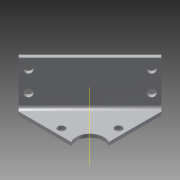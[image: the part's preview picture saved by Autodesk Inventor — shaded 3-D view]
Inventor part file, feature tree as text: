
AUTODESK INVENTOR PART (.ipt)
format: ipt  version: 2013 (Build 170138000, 138)  size: 141,824 bytes
history: native  units: in
note: dims shown in document units (in); Inventor stores cm internally (conversion verified against a paired STEP export)
features: sheet_metal_op x4, other x4, sketch x3
ambient origin geometry x8: Origin, YZ Plane, XZ Plane, XY Plane, X Axis, Y Axis, Z Axis, Center Point
bodies: Solid1 (feature_tree)
feature tree (11):
  sheet_metal_op  "Face1"
  sheet_metal_op  "Flange1"
  sketch  "Sketch3"  dims[d2=0.26in d3=0.26in d4=0.26in d5=1.0in d8=0.25in d9=0.0in d10=0.25in d11=0.25in d12=45.0deg d13=0.75in d14=0.125in d15=0.125in d16=0.0625in d17=0.25in d18=0.125in d19=1.75in d20=90.0deg d21=0.125in d22=0.5in d23=0.125in d24=0.125in d35=3.685in d36=0.266in d37=0.266in d38=0.266in d39=0.266in d40=0.25in d41=0.375in d42=0.375in d43=0.25in d44=0.375in d45=0.375in d47=0.25in d48=0.25in d49=0.125in d50=0.0in]
  other  "Work Axis1"
  sketch  "Sketch1"  dims[d0=2.09in]
  other  "Plate1"
  sketch  "Sketch2"  dims[d1=0.26in]
  other  "Plate2"
  sheet_metal_op  "Bend1"
  sheet_metal_op  "Corner1"
  other  "Cut3"
